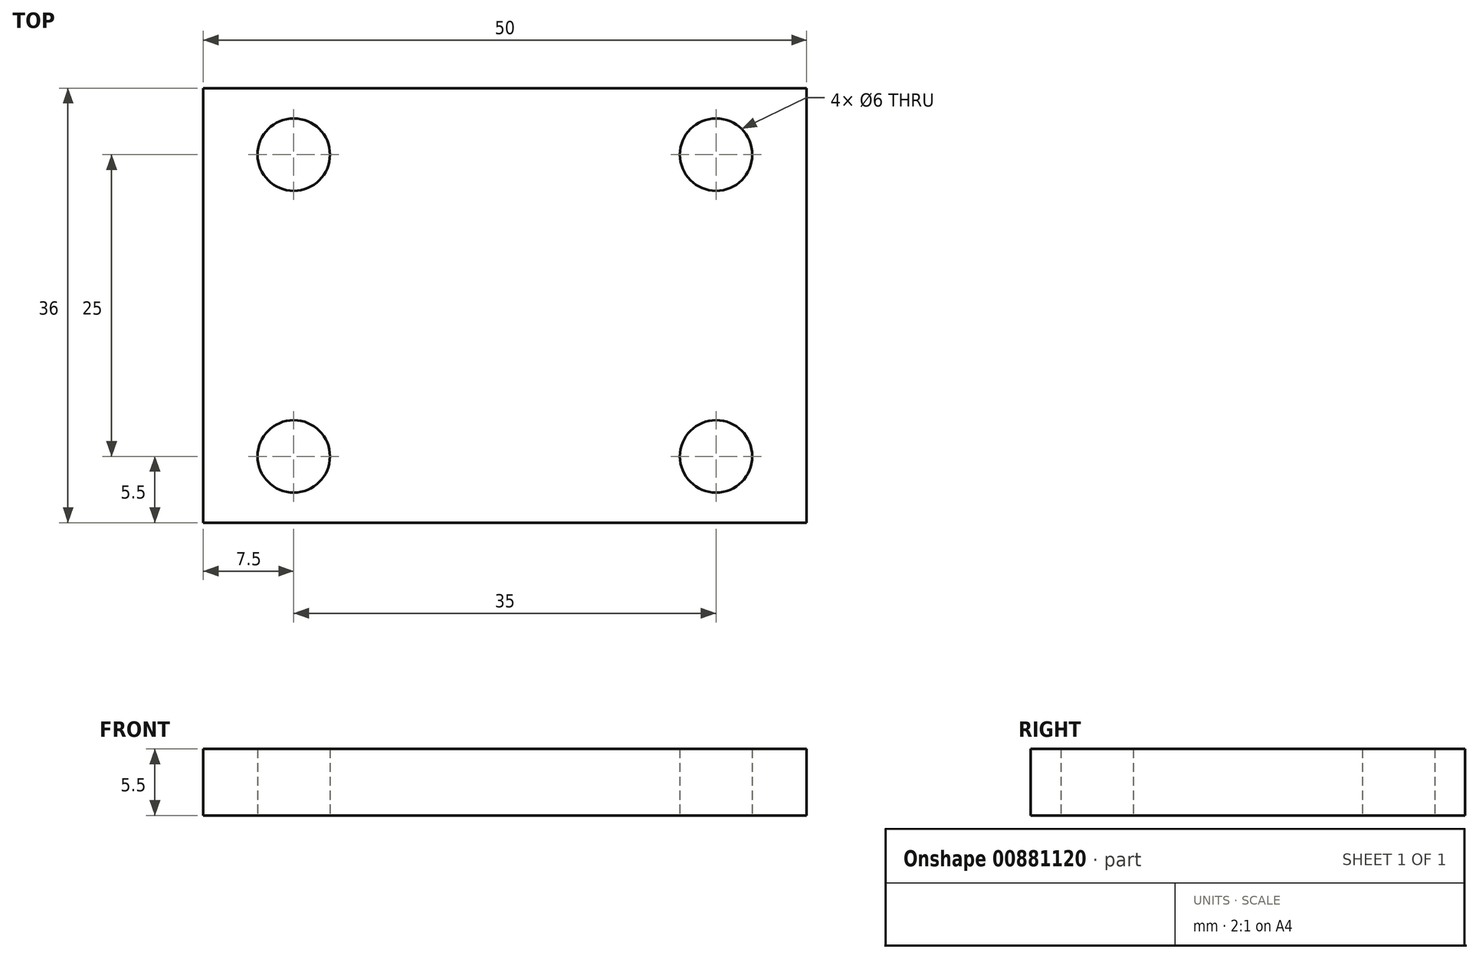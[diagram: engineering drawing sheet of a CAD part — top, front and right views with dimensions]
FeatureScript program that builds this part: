
annotation { "Feature Type Name" : "Feature", "Feature Type Description" : "" }
export const myFeature = defineFeature(function(context is Context, id is Id, definition is map)
    precondition{}
    {
        {
            var Q0;
            Q0=qCreatedBy(makeId("Top.planeOp"),FACE);
            var sketch = newSketch(context, id + "F0", { "sketchPlane" : qUnion([Q0])});
            skLineSegment(sketch, "E0.bottom", {"start": v(0, 0) * mm, "end": v(50, 0) * mm});
            skLineSegment(sketch, "E0.top", {"start": v(0, 36) * mm, "end": v(50, 36) * mm});
            skLineSegment(sketch, "E0.left", {"start": v(0, 0) * mm, "end": v(0, 36) * mm});
            skLineSegment(sketch, "E0.right", {"start": v(50, 0) * mm, "end": v(50, 36) * mm});
            skCircle(sketch, "E1", {"center": v(7.5, 30.5) * mm, "radius": 3 * mm});
            skCircle(sketch, "E2", {"center": v(7.5, 5.5) * mm, "radius": 3 * mm});
            skCircle(sketch, "E3", {"center": v(42.5, 30.5) * mm, "radius": 3 * mm});
            skCircle(sketch, "E4", {"center": v(42.5, 5.5) * mm, "radius": 3 * mm});
            skSolve(sketch);
        }
        {
            var Q0;
            Q0=makeQuery(id+"F0.imprint","IMPRINT",FACE,{"disambiguationData":[TD([[makeQuery(id+"F0.imprint","IMPRINT",EDGE,{"derivedFrom":sQuery(id+"F0.wireOp",EDGE,"E0.bottom")}),1.0]])]});
            extrude(context, id + "F1", {"entities" : qUnion([Q0]), "depth" : 5.5 * mm, "offsetDistance" : 25 * mm});
        }
    });
